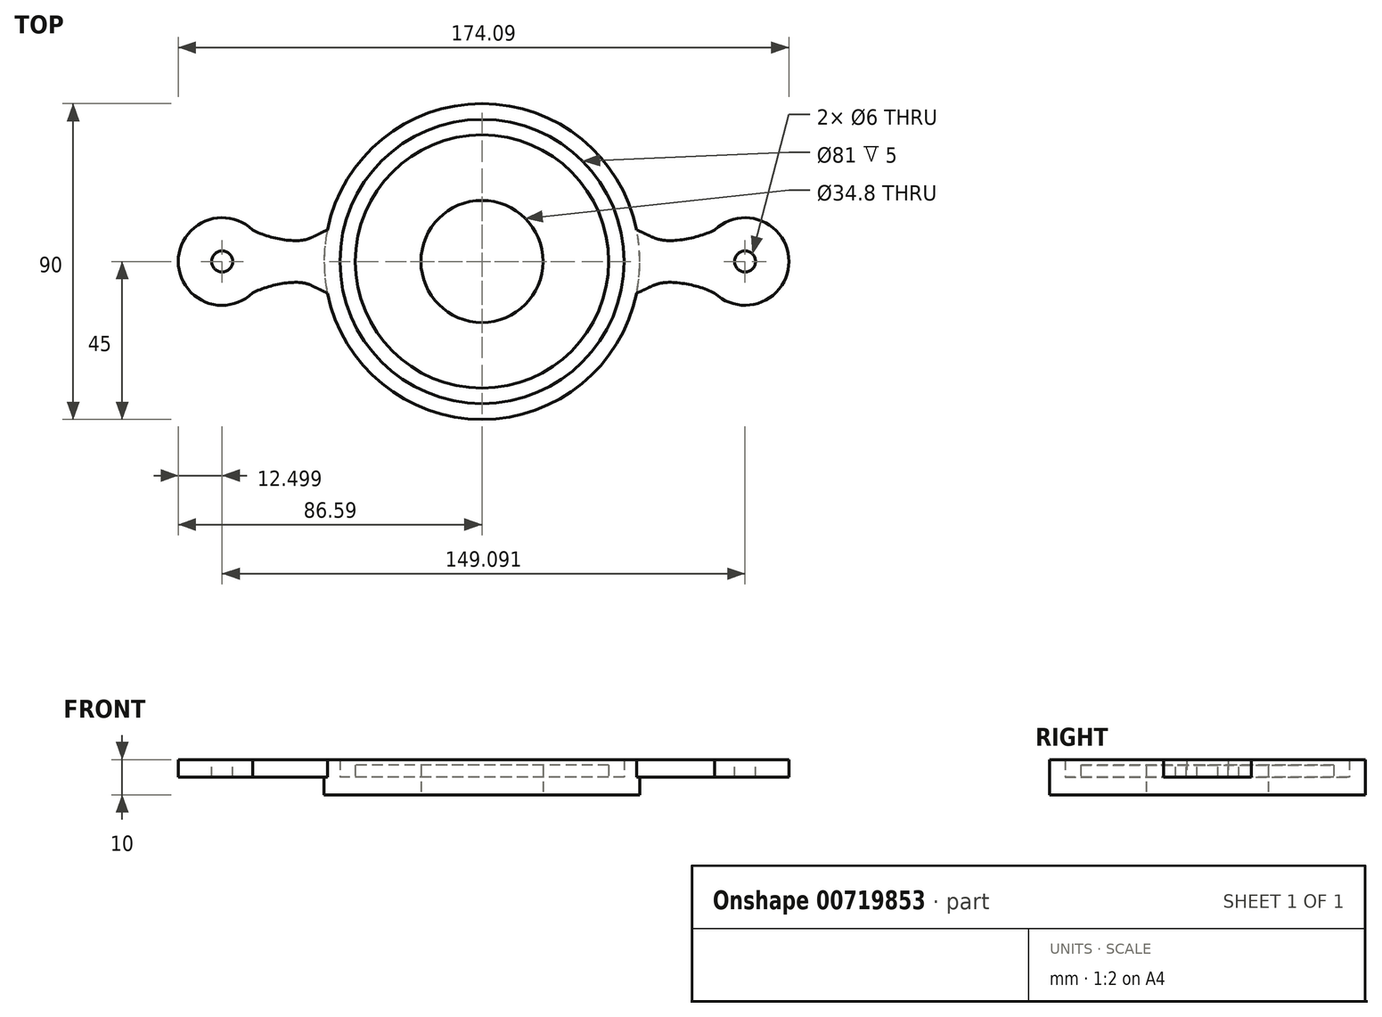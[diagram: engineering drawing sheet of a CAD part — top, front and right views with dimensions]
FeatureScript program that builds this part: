
annotation { "Feature Type Name" : "Feature", "Feature Type Description" : "" }
export const myFeature = defineFeature(function(context is Context, id is Id, definition is map)
    precondition{}
    {
        {
            var Q0;
            Q0=qCreatedBy(makeId("Top.planeOp"),FACE);
            var sketch = newSketch(context, id + "F0", { "sketchPlane" : qUnion([Q0])});
            skCircle(sketch, "E0", {"center": v(0, 0) * mm, "radius": 45 * mm});
            skCircle(sketch, "E1", {"center": v(0, 0) * mm, "radius": 40.5 * mm});
            skCircle(sketch, "E2", {"center": v(0, 0) * mm, "radius": 36.1 * mm});
            skCircle(sketch, "E3", {"center": v(0, 0) * mm, "radius": 31 * mm});
            skCircle(sketch, "E4", {"center": v(0, 0) * mm, "radius": 17.4 * mm});
            skCircle(sketch, "E5", {"center": v(0, 0) * mm, "radius": 9 * mm});
            skCircle(sketch, "E6", {"center": v(0, 0) * mm, "radius": 5 * mm});
            skSolve(sketch);
        }
        {
            var Q0;
            Q0=makeQuery(id+"F0.imprint","IMPRINT",FACE,{"disambiguationData":[TD([[makeQuery(id+"F0.imprint","IMPRINT",EDGE,{"derivedFrom":sQuery(id+"F0.wireOp",EDGE,"E0")}),1.0]])]});
            extrude(context, id + "F1", {"entities" : qUnion([Q0]), "depth" : 10 * mm, "offsetDistance" : 25 * mm});
        }
        {
            var Q0;
            Q0=makeQuery(id+"F0.imprint","IMPRINT",FACE,{"disambiguationData":[TD([[makeQuery(id+"F0.imprint","IMPRINT",EDGE,{"derivedFrom":sQuery(id+"F0.wireOp",EDGE,"E1")}),1.0]])]});
            extrude(context, id + "F2", {"entities" : qUnion([Q0]), "operationType" : NewBodyOperationType.ADD, "depth" : 5 * mm, "offsetDistance" : 25 * mm});
        }
        {
            var Q0;
            Q0=makeQuery(id+"F0.imprint","IMPRINT",FACE,{"disambiguationData":[TD([[makeQuery(id+"F0.imprint","IMPRINT",EDGE,{"derivedFrom":sQuery(id+"F0.wireOp",EDGE,"E2")}),1.0]])]});
            extrude(context, id + "F3", {"entities" : qUnion([Q0]), "operationType" : NewBodyOperationType.ADD, "depth" : 8.4 * mm, "offsetDistance" : 25 * mm});
        }
        {
            var Q0;
            Q0=makeQuery(id+"F0.imprint","IMPRINT",FACE,{"disambiguationData":[TD([[makeQuery(id+"F0.imprint","IMPRINT",EDGE,{"derivedFrom":sQuery(id+"F0.wireOp",EDGE,"E3")}),1.0]])]});
            extrude(context, id + "F4", {"entities" : qUnion([Q0]), "operationType" : NewBodyOperationType.ADD, "depth" : 8.4 * mm, "offsetDistance" : 25 * mm});
        }
        {
            var Q0;
            Q0=makeQuery(id+"F1.opExtrude","CAP_FACE",FACE,{"disambiguationData":[OSD([sQuery(id+"F0.wireOp",EDGE,"E0"),sQuery(id+"F0.wireOp",EDGE,"E1")])],"isStart":false});
            var sketch = newSketch(context, id + "F5", { "sketchPlane" : qUnion([Q0])});
            skCircle(sketch, "E7", {"center": v(75, 0) * mm, "radius": 12.5 * mm});
            skFitSpline(sketch, "E8", {"points": [v(66.33, -9) * mm, v(52.21, -6) * mm, v(44.1, -9) * mm], "startDerivative": vector(-20.09, 10.5) * mm, "endDerivative": vector(-23.83, -9.68) * mm});
            skFitSpline(sketch, "E9", {"points": [v(66.33, 9) * mm, v(52.21, 6) * mm, v(44.1, 9) * mm], "startDerivative": vector(-20.09, -10.5) * mm, "endDerivative": vector(-23.83, 9.68) * mm});
            skLineSegment(sketch, "E10", {"start": v(75, 0) * mm, "end": v(45, 0) * mm});
            skLineSegment(sketch, "E11", {"start": v(52.21, -6) * mm, "end": v(52.21, 0) * mm});
            skLineSegment(sketch, "E12", {"start": v(52.21, 6) * mm, "end": v(52.21, 0) * mm});
            skLineSegment(sketch, "E13", {"start": v(66.33, -9) * mm, "end": v(66.33, 0) * mm});
            skLineSegment(sketch, "E14", {"start": v(66.33, 0) * mm, "end": v(66.33, 9) * mm});
            skLineSegment(sketch, "E15", {"start": v(45, 0) * mm, "end": v(0, 0) * mm});
            skLineSegment(sketch, "E16", {"start": v(44.1, -9) * mm, "end": v(44.1, 0) * mm});
            skLineSegment(sketch, "E17", {"start": v(44.1, 0) * mm, "end": v(44.1, 9) * mm});
            skLineSegment(sketch, "E18", {"start": v(47.56, -7.6) * mm, "end": v(47.56, 0) * mm});
            skLineSegment(sketch, "E19", {"start": v(47.56, 0) * mm, "end": v(47.56, 7.6) * mm});
            skLineSegment(sketch, "E20", {"start": v(62.55, -7.03) * mm, "end": v(62.55, 0) * mm});
            skLineSegment(sketch, "E21", {"start": v(62.55, 0) * mm, "end": v(62.55, 7.03) * mm});
            skCircle(sketch, "E22", {"center": v(75, 0) * mm, "radius": 3 * mm});
            skCircle(sketch, "E23", {"center": v(-74.1, 0) * mm, "radius": 12.5 * mm});
            skFitSpline(sketch, "E24", {"points": [v(-65.42, 9) * mm, v(-51.7, 6) * mm, v(-44.1, 9) * mm], "startDerivative": vector(19.75, -10.87) * mm, "endDerivative": vector(23.53, 10.09) * mm});
            skFitSpline(sketch, "E25", {"points": [v(-65.41, -9) * mm, v(-51.7, -6) * mm, v(-44.1, -9) * mm], "startDerivative": vector(19.72, 10.84) * mm, "endDerivative": vector(23.53, -10.09) * mm});
            skLineSegment(sketch, "E26", {"start": v(-74.1, 0) * mm, "end": v(-11.07, 0) * mm});
            skLineSegment(sketch, "E27", {"start": v(-51.7, 6) * mm, "end": v(-51.7, 0) * mm});
            skLineSegment(sketch, "E28", {"start": v(-51.7, -6) * mm, "end": v(-51.7, 0) * mm});
            skLineSegment(sketch, "E29", {"start": v(-65.42, 9) * mm, "end": v(-65.42, 0) * mm});
            skLineSegment(sketch, "E30", {"start": v(-65.42, 0) * mm, "end": v(-65.41, -9) * mm});
            skLineSegment(sketch, "E31", {"start": v(-11.07, 0) * mm, "end": v(0, 0) * mm});
            skLineSegment(sketch, "E32", {"start": v(-44.1, 9) * mm, "end": v(-44.1, 0) * mm});
            skLineSegment(sketch, "E33", {"start": v(-44.1, 0) * mm, "end": v(-44.1, -9) * mm});
            skLineSegment(sketch, "E34", {"start": v(-47.49, 7.54) * mm, "end": v(-47.49, 0) * mm});
            skLineSegment(sketch, "E35", {"start": v(-47.49, 0) * mm, "end": v(-47.49, -7.54) * mm});
            skLineSegment(sketch, "E36", {"start": v(-61.69, 6.95) * mm, "end": v(-61.69, 0) * mm});
            skLineSegment(sketch, "E37", {"start": v(-61.69, 0) * mm, "end": v(-61.69, -6.95) * mm});
            skCircle(sketch, "E38", {"center": v(-74.1, 0) * mm, "radius": 3 * mm});
            skSolve(sketch);
        }
        {
            var Q0;
            {var subQ0=sQuery(id+"F5.wireOp",EDGE,"E13");Q0=makeQuery(id+"F5.imprint","IMPRINT",FACE,{"disambiguationData":[TD([[makeQuery(id+"F5.imprint","IMPRINT",EDGE,{"derivedFrom":subQ0}),-1.0]])]});}
            var Q1;
            {var subQ0=sQuery(id+"F5.wireOp",EDGE,"E13");Q1=makeQuery(id+"F5.imprint","IMPRINT",FACE,{"disambiguationData":[TD([[makeQuery(id+"F5.imprint","IMPRINT",EDGE,{"derivedFrom":subQ0}),1.0]])]});}
            var Q2;
            {var subQ0=sQuery(id+"F5.wireOp",EDGE,"E14");Q2=makeQuery(id+"F5.imprint","IMPRINT",FACE,{"disambiguationData":[TD([[makeQuery(id+"F5.imprint","IMPRINT",EDGE,{"derivedFrom":subQ0}),1.0]])]});}
            var Q3;
            {var subQ0=sQuery(id+"F5.wireOp",EDGE,"E12");Q3=makeQuery(id+"F5.imprint","IMPRINT",FACE,{"disambiguationData":[TD([[makeQuery(id+"F5.imprint","IMPRINT",EDGE,{"derivedFrom":subQ0}),1.0]])]});}
            var Q4;
            {var subQ0=sQuery(id+"F5.wireOp",EDGE,"E11");Q4=makeQuery(id+"F5.imprint","IMPRINT",FACE,{"disambiguationData":[TD([[makeQuery(id+"F5.imprint","IMPRINT",EDGE,{"derivedFrom":subQ0}),1.0]])]});}
            var Q5;
            {var subQ0=sQuery(id+"F5.wireOp",EDGE,"E21");var subQ1=sQuery(id+"F5.wireOp",EDGE,"E7");var subQ2=makeQuery(id+"F5.imprint","INTERSECT",VERTEX,{"derivedFrom":[subQ1,subQ0]});Q5=makeQuery(id+"F5.imprint","IMPRINT",FACE,{"disambiguationData":[TD([[makeQuery(id+"F5.imprint","IMPRINT",EDGE,{"disambiguationData":[TD([[subQ2,-1.0]])],"derivedFrom":subQ1}),1.0]])]});}
            var Q6;
            {var subQ0=sQuery(id+"F5.wireOp",EDGE,"E20");var subQ1=sQuery(id+"F5.wireOp",EDGE,"E7");var subQ2=makeQuery(id+"F5.imprint","INTERSECT",VERTEX,{"derivedFrom":[subQ1,subQ0]});Q6=makeQuery(id+"F5.imprint","IMPRINT",FACE,{"disambiguationData":[TD([[makeQuery(id+"F5.imprint","IMPRINT",EDGE,{"disambiguationData":[TD([[subQ2,1.0]])],"derivedFrom":subQ1}),1.0]])]});}
            var Q7;
            {var subQ3=sQuery(id+"F5.wireOp",EDGE,"E11");Q7=makeQuery(id+"F5.imprint","IMPRINT",FACE,{"disambiguationData":[TD([[makeQuery(id+"F5.imprint","IMPRINT",EDGE,{"derivedFrom":subQ3}),-1.0]])]});}
            var Q8;
            {var subQ0=sQuery(id+"F5.wireOp",EDGE,"E12");Q8=makeQuery(id+"F5.imprint","IMPRINT",FACE,{"disambiguationData":[TD([[makeQuery(id+"F5.imprint","IMPRINT",EDGE,{"derivedFrom":subQ0}),-1.0]])]});}
            var Q9;
            {var subQ0=sQuery(id+"F5.wireOp",EDGE,"E8");var subQ3=sQuery(id+"F5.wireOp",EDGE,"E18");var subQ4=makeQuery(id+"F5.imprint","INTERSECT",VERTEX,{"derivedFrom":[subQ0,subQ3]});Q9=makeQuery(id+"F5.imprint","IMPRINT",FACE,{"disambiguationData":[TD([[makeQuery(id+"F5.imprint","IMPRINT",EDGE,{"disambiguationData":[TD([[subQ4,-1.0]])],"derivedFrom":subQ0}),-1.0]])]});}
            var Q10;
            {var subQ0=sQuery(id+"F5.wireOp",EDGE,"E9");var subQ3=sQuery(id+"F5.wireOp",EDGE,"E19");var subQ4=makeQuery(id+"F5.imprint","INTERSECT",VERTEX,{"derivedFrom":[subQ0,subQ3]});Q10=makeQuery(id+"F5.imprint","IMPRINT",FACE,{"disambiguationData":[TD([[makeQuery(id+"F5.imprint","IMPRINT",EDGE,{"disambiguationData":[TD([[subQ4,-1.0]])],"derivedFrom":subQ0}),1.0]])]});}
            var Q11;
            {var subQ4=sQuery(id+"F5.wireOp",EDGE,"E16");Q11=makeQuery(id+"F5.imprint","IMPRINT",FACE,{"disambiguationData":[TD([[makeQuery(id+"F5.imprint","IMPRINT",EDGE,{"derivedFrom":subQ4}),1.0]])]});}
            var Q12;
            Q12=makeQuery(id+"F1.opExtrude","CAP_FACE",FACE,{"disambiguationData":[OSD([sQuery(id+"F0.wireOp",EDGE,"E0"),sQuery(id+"F0.wireOp",EDGE,"E1")])],"isStart":false});
            var Q13;
            {var subQ3=sQuery(id+"F5.wireOp",EDGE,"E27");Q13=makeQuery(id+"F5.imprint","IMPRINT",FACE,{"disambiguationData":[TD([[makeQuery(id+"F5.imprint","IMPRINT",EDGE,{"derivedFrom":subQ3}),-1.0]])]});}
            var Q14;
            {var subQ0=sQuery(id+"F5.wireOp",EDGE,"E33");Q14=makeQuery(id+"F5.imprint","IMPRINT",FACE,{"disambiguationData":[TD([[makeQuery(id+"F5.imprint","IMPRINT",EDGE,{"derivedFrom":subQ0}),-1.0]])]});}
            var Q15;
            {var subQ0=sQuery(id+"F5.wireOp",EDGE,"E28");Q15=makeQuery(id+"F5.imprint","IMPRINT",FACE,{"disambiguationData":[TD([[makeQuery(id+"F5.imprint","IMPRINT",EDGE,{"derivedFrom":subQ0}),1.0]])]});}
            var Q16;
            {var subQ0=sQuery(id+"F5.wireOp",EDGE,"E28");Q16=makeQuery(id+"F5.imprint","IMPRINT",FACE,{"disambiguationData":[TD([[makeQuery(id+"F5.imprint","IMPRINT",EDGE,{"derivedFrom":subQ0}),-1.0]])]});}
            var Q17;
            {var subQ1=sQuery(id+"F5.wireOp",EDGE,"E29");Q17=makeQuery(id+"F5.imprint","IMPRINT",FACE,{"disambiguationData":[TD([[makeQuery(id+"F5.imprint","IMPRINT",EDGE,{"derivedFrom":subQ1}),1.0]])]});}
            var Q18;
            {var subQ1=sQuery(id+"F5.wireOp",EDGE,"E23");var subQ3=sQuery(id+"F5.wireOp",EDGE,"E37");var subQ4=makeQuery(id+"F5.imprint","INTERSECT",VERTEX,{"derivedFrom":[subQ1,subQ3]});Q18=makeQuery(id+"F5.imprint","IMPRINT",FACE,{"disambiguationData":[TD([[makeQuery(id+"F5.imprint","IMPRINT",EDGE,{"disambiguationData":[TD([[subQ4,1.0]])],"derivedFrom":subQ1}),1.0]])]});}
            var Q19;
            {var subQ0=sQuery(id+"F5.wireOp",EDGE,"E25");var subQ3=sQuery(id+"F5.wireOp",EDGE,"E35");var subQ4=makeQuery(id+"F5.imprint","INTERSECT",VERTEX,{"derivedFrom":[subQ0,subQ3]});Q19=makeQuery(id+"F5.imprint","IMPRINT",FACE,{"disambiguationData":[TD([[makeQuery(id+"F5.imprint","IMPRINT",EDGE,{"disambiguationData":[TD([[subQ4,-1.0]])],"derivedFrom":subQ0}),1.0]])]});}
            var Q20;
            {var subQ0=sQuery(id+"F5.wireOp",EDGE,"E24");var subQ3=sQuery(id+"F5.wireOp",EDGE,"E34");var subQ4=makeQuery(id+"F5.imprint","INTERSECT",VERTEX,{"derivedFrom":[subQ0,subQ3]});Q20=makeQuery(id+"F5.imprint","IMPRINT",FACE,{"disambiguationData":[TD([[makeQuery(id+"F5.imprint","IMPRINT",EDGE,{"disambiguationData":[TD([[subQ4,-1.0]])],"derivedFrom":subQ0}),-1.0]])]});}
            var Q21;
            {var subQ0=sQuery(id+"F5.wireOp",EDGE,"E32");Q21=makeQuery(id+"F5.imprint","IMPRINT",FACE,{"disambiguationData":[TD([[makeQuery(id+"F5.imprint","IMPRINT",EDGE,{"derivedFrom":subQ0}),-1.0]])]});}
            var Q22;
            {var subQ0=sQuery(id+"F5.wireOp",EDGE,"E37");var subQ1=sQuery(id+"F5.wireOp",EDGE,"E23");var subQ2=makeQuery(id+"F5.imprint","INTERSECT",VERTEX,{"derivedFrom":[subQ1,subQ0]});Q22=makeQuery(id+"F5.imprint","IMPRINT",FACE,{"disambiguationData":[TD([[makeQuery(id+"F5.imprint","IMPRINT",EDGE,{"disambiguationData":[TD([[subQ2,-1.0]])],"derivedFrom":subQ1}),1.0]])]});}
            var Q23;
            {var subQ0=sQuery(id+"F5.wireOp",EDGE,"E36");var subQ1=sQuery(id+"F5.wireOp",EDGE,"E23");var subQ2=makeQuery(id+"F5.imprint","INTERSECT",VERTEX,{"derivedFrom":[subQ1,subQ0]});Q23=makeQuery(id+"F5.imprint","IMPRINT",FACE,{"disambiguationData":[TD([[makeQuery(id+"F5.imprint","IMPRINT",EDGE,{"disambiguationData":[TD([[subQ2,1.0]])],"derivedFrom":subQ1}),1.0]])]});}
            var Q24;
            {var subQ0=sQuery(id+"F5.wireOp",EDGE,"E27");Q24=makeQuery(id+"F5.imprint","IMPRINT",FACE,{"disambiguationData":[TD([[makeQuery(id+"F5.imprint","IMPRINT",EDGE,{"derivedFrom":subQ0}),1.0]])]});}
            var Q25;
            {var subQ4=sQuery(id+"F5.wireOp",EDGE,"E29");Q25=makeQuery(id+"F5.imprint","IMPRINT",FACE,{"disambiguationData":[TD([[makeQuery(id+"F5.imprint","IMPRINT",EDGE,{"derivedFrom":subQ4}),-1.0]])]});}
            extrude(context, id + "F6", {"entities" : qUnion([Q0, Q1, Q2, Q3, Q4, Q5, Q6, Q7, Q8, Q9, Q10, Q11, Q12, Q13, Q14, Q15, Q16, Q17, Q18, Q19, Q20, Q21, Q22, Q23, Q24, Q25]), "operationType" : NewBodyOperationType.ADD, "oppositeDirection" : true, "depth" : 5 * mm, "offsetDistance" : 25 * mm});
        }
    });
